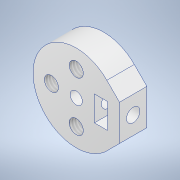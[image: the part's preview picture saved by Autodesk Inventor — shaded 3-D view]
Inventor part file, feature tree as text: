
AUTODESK INVENTOR PART (.ipt)
format: ipt  version: 2022 (Build 260153000, 153)  size: 162,304 bytes
history: native  units: mm
features: sketch x3, extrude x2, hole x2, pattern_circular x1
ambient origin geometry x8: Origin, YZ Plane, XZ Plane, XY Plane, X Axis, Y Axis, Z Axis, Center Point
bodies: Solid1 (feature_tree)
feature tree (8):
  extrude  "Extrusion1"  Depth=20.0mm
  hole  "Hole1"  [1 undecoded]
  pattern_circular  "Circular Pattern1"  [2 undecoded]
  extrude  "Extrusion3"  Depth=10.0mm
  hole  "Hole3"  [1 undecoded]
  sketch  "Sketch2"  dims[d0=2.8mm d1=20.0mm]
  sketch  "Sketch5"  dims[d2=6.35mm d3=0.0mm]
  sketch  "Sketch6"  dims[d5=3.242mm d6=8.0mm d7=6.3mm d8=2.0mm d9=90.0deg d10=8.0mm d11=20.594885mm d12=40.0mm d13=360.0deg d28=5.8mm d29=3.0mm d30=10.0mm d31=0.0mm d33=135.0deg d34=4.25mm d35=3.1mm d36=6.0mm d37=6.3mm d38=2.0mm d39=90.0deg d40=10.0mm d41=0.0mm]
note: 4 required parameter values undecoded (feature->parameter linkage not recoverable at this tier; creation-order binding heuristic only, values carry confidence <= 0.55)
